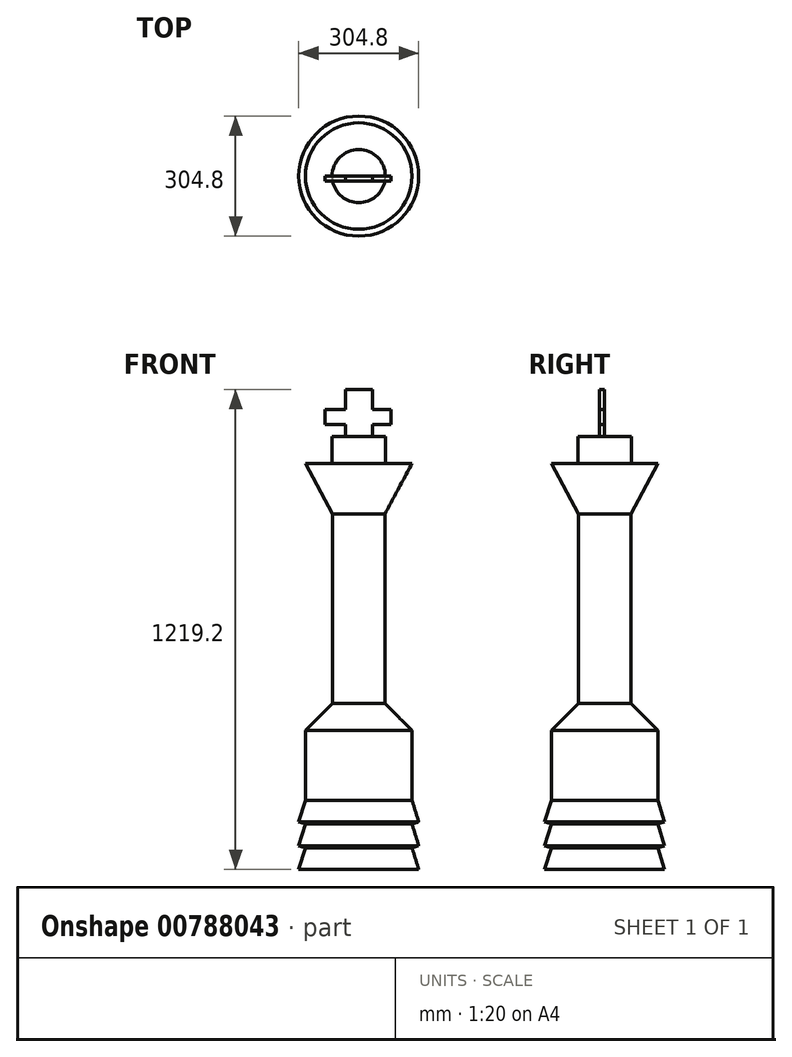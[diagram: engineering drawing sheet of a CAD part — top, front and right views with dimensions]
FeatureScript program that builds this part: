
annotation { "Feature Type Name" : "Feature", "Feature Type Description" : "" }
export const myFeature = defineFeature(function(context is Context, id is Id, definition is map)
    precondition{}
    {
        {
            var Q0;
            Q0=qCreatedBy(makeId("Front.planeOp"),FACE);
            var sketch = newSketch(context, id + "F0", { "sketchPlane" : qUnion([Q0])});
            skLineSegment(sketch, "E0", {"start": v(0, -841.35) * mm, "end": v(-152.4, -841.35) * mm});
            skLineSegment(sketch, "E1", {"start": v(-152.4, -841.35) * mm, "end": v(-135.26, -786.33) * mm});
            skLineSegment(sketch, "E2", {"start": v(-135.26, -786.33) * mm, "end": v(-152.4, -780.99) * mm});
            skLineSegment(sketch, "E3", {"start": v(-152.4, -780.99) * mm, "end": v(-135.26, -725.97) * mm});
            skLineSegment(sketch, "E4", {"start": v(-135.26, -725.97) * mm, "end": v(-152.4, -720.62) * mm});
            skLineSegment(sketch, "E5", {"start": v(-152.4, -720.62) * mm, "end": v(-135.26, -665.6) * mm});
            skLineSegment(sketch, "E6", {"start": v(-135.26, -665.6) * mm, "end": v(-135.26, -488.3) * mm});
            skLineSegment(sketch, "E7", {"start": v(-135.26, -488.3) * mm, "end": v(-66.48, -419.53) * mm});
            skLineSegment(sketch, "E8", {"start": v(-66.48, -419.53) * mm, "end": v(-66.48, 61.9) * mm});
            skLineSegment(sketch, "E9", {"start": v(-66.48, 61.9) * mm, "end": v(-135.26, 190.28) * mm});
            skLineSegment(sketch, "E10", {"start": v(-135.26, 190.28) * mm, "end": v(0, 190.28) * mm});
            skLineSegment(sketch, "E11", {"start": v(-67.63, 190.28) * mm, "end": v(-67.63, 259.05) * mm});
            skLineSegment(sketch, "E12", {"start": v(-67.63, 259.05) * mm, "end": v(0, 259.05) * mm});
            skLineSegment(sketch, "E13", {"start": v(0, 1166.88) * mm, "end": v(0, -1364.04) * mm});
            skLineSegment(sketch, "E14", {"start": v(-33.81, 259.05) * mm, "end": v(-33.81, 288.49) * mm});
            skLineSegment(sketch, "E15", {"start": v(-33.81, 288.49) * mm, "end": v(-85.77, 288.49) * mm});
            skLineSegment(sketch, "E16", {"start": v(-85.77, 288.49) * mm, "end": v(-85.77, 327.25) * mm});
            skLineSegment(sketch, "E17", {"start": v(-85.77, 327.25) * mm, "end": v(-33.81, 327.25) * mm});
            skLineSegment(sketch, "E18", {"start": v(-33.81, 327.25) * mm, "end": v(-33.81, 377.85) * mm});
            skLineSegment(sketch, "E19", {"start": v(-33.81, 377.85) * mm, "end": v(0, 377.85) * mm});
            skLineSegment(sketch, "E20", {"start": v(0, 377.85) * mm, "end": v(34.83, 377.85) * mm});
            skLineSegment(sketch, "E21", {"start": v(34.83, 377.85) * mm, "end": v(34.83, 327.25) * mm});
            skLineSegment(sketch, "E22", {"start": v(34.83, 327.25) * mm, "end": v(82.2, 327.25) * mm});
            skLineSegment(sketch, "E23", {"start": v(82.2, 327.25) * mm, "end": v(82.2, 288.49) * mm});
            skLineSegment(sketch, "E24", {"start": v(82.2, 288.49) * mm, "end": v(34.83, 288.49) * mm});
            skLineSegment(sketch, "E25", {"start": v(34.83, 288.49) * mm, "end": v(34.83, 259.05) * mm});
            skLineSegment(sketch, "E26", {"start": v(34.83, 259.05) * mm, "end": v(0, 259.05) * mm});
            skLineSegment(sketch, "E27", {"start": v(-152.4, -841.35) * mm, "end": v(-146.32, -821.83) * mm});
            skLineSegment(sketch, "E28", {"start": v(-146.32, -821.83) * mm, "end": v(-135.26, -786.33) * mm});
            skLineSegment(sketch, "E29", {"start": v(-152.4, -841.35) * mm, "end": v(-152.4, -804.08) * mm});
            skPoint(sketch, "E29.endSnap0", {"position": v(-140.79, -804.08) * mm});
            skLineSegment(sketch, "E30", {"start": v(-152.4, -804.08) * mm, "end": v(-135.26, -786.33) * mm});
            skSolve(sketch);
        }
        {
            var Q0;
            {var subQ4=sQuery(id+"F0.wireOp",EDGE,"E11");Q0=makeQuery(id+"F0.imprint","IMPRINT",FACE,{"disambiguationData":[TD([[makeQuery(id+"F0.imprint","IMPRINT",EDGE,{"derivedFrom":subQ4}),-1.0]])]});}
            var Q1;
            {var subQ0=sQuery(id+"F0.wireOp",EDGE,"E0");Q1=makeQuery(id+"F0.imprint","IMPRINT",FACE,{"disambiguationData":[TD([[makeQuery(id+"F0.imprint","IMPRINT",EDGE,{"derivedFrom":subQ0}),-1.0]])]});}
            var Q2;
            Q2=sQuery(id+"F0.wireOp",EDGE,"E13");
            revolve(context, id + "F1", {"surfaceOperationType" : NewSurfaceOperationType.NEW, "entities" : qUnion([Q0, Q1]), "axis" : qUnion([Q2]), "revolveType" : RevolveType.FULL});
        }
        {
            var Q0;
            {var subQ0=sQuery(id+"F0.wireOp",EDGE,"E14");Q0=makeQuery(id+"F0.imprint","IMPRINT",FACE,{"disambiguationData":[TD([[makeQuery(id+"F0.imprint","IMPRINT",EDGE,{"derivedFrom":subQ0}),-1.0]])]});}
            var Q1;
            {var subQ0=sQuery(id+"F0.wireOp",EDGE,"E20");Q1=makeQuery(id+"F0.imprint","IMPRINT",FACE,{"disambiguationData":[TD([[makeQuery(id+"F0.imprint","IMPRINT",EDGE,{"derivedFrom":subQ0}),-1.0]])]});}
            extrude(context, id + "F2", {"entities" : qUnion([Q0, Q1]), "operationType" : NewBodyOperationType.ADD, "depth" : 12.7 * mm, "offsetDistance" : 25.4 * mm});
        }
    });
